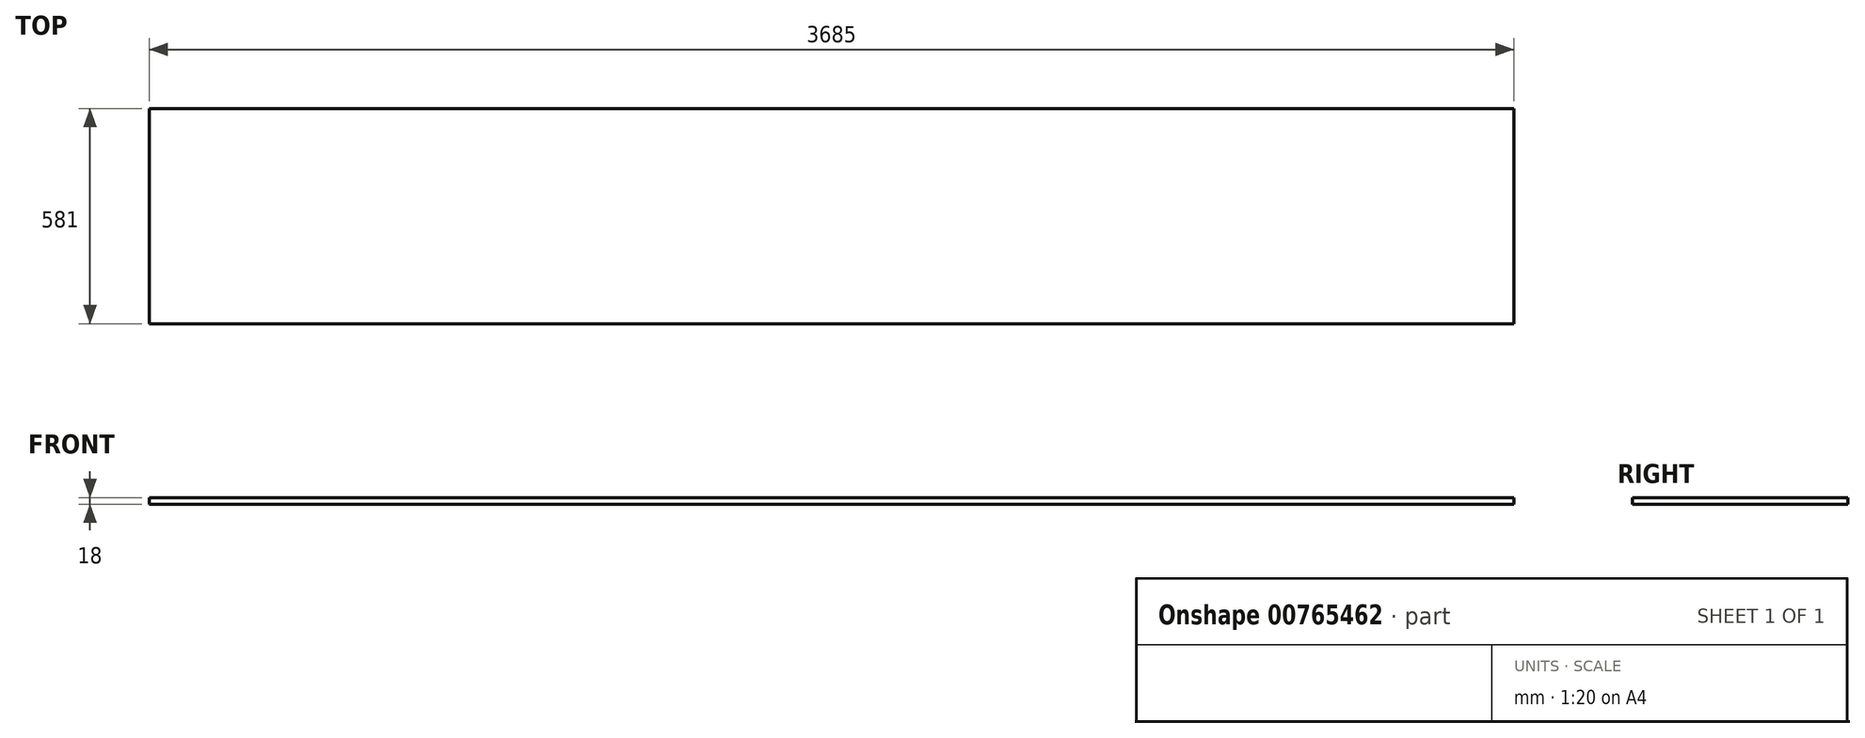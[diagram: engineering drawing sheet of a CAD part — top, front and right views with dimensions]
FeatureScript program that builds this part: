
annotation { "Feature Type Name" : "Feature", "Feature Type Description" : "" }
export const myFeature = defineFeature(function(context is Context, id is Id, definition is map)
    precondition{}
    {
        {
            var Q0;
            Q0=qCreatedBy(makeId("Top.planeOp"),FACE);
            var sketch = newSketch(context, id + "F0", { "sketchPlane" : qUnion([Q0])});
            skLineSegment(sketch, "E0.bottom", {"start": v(-1842.5, -290.5) * mm, "end": v(1842.5, -290.5) * mm});
            skLineSegment(sketch, "E0.top", {"start": v(-1842.5, 290.5) * mm, "end": v(1842.5, 290.5) * mm});
            skLineSegment(sketch, "E0.left", {"start": v(-1842.5, -290.5) * mm, "end": v(-1842.5, 290.5) * mm});
            skLineSegment(sketch, "E0.right", {"start": v(1842.5, -290.5) * mm, "end": v(1842.5, 290.5) * mm});
            skPoint(sketch, "E0.middle", {"position": v(0, 0) * mm});
            skSolve(sketch);
        }
        {
            var Q0;
            Q0 = qSketchRegion(id + "F0", true);
            extrude(context, id + "F1", {"entities" : qUnion([Q0]), "depth" : 18 * mm, "offsetDistance" : 25 * mm});
        }
    });
